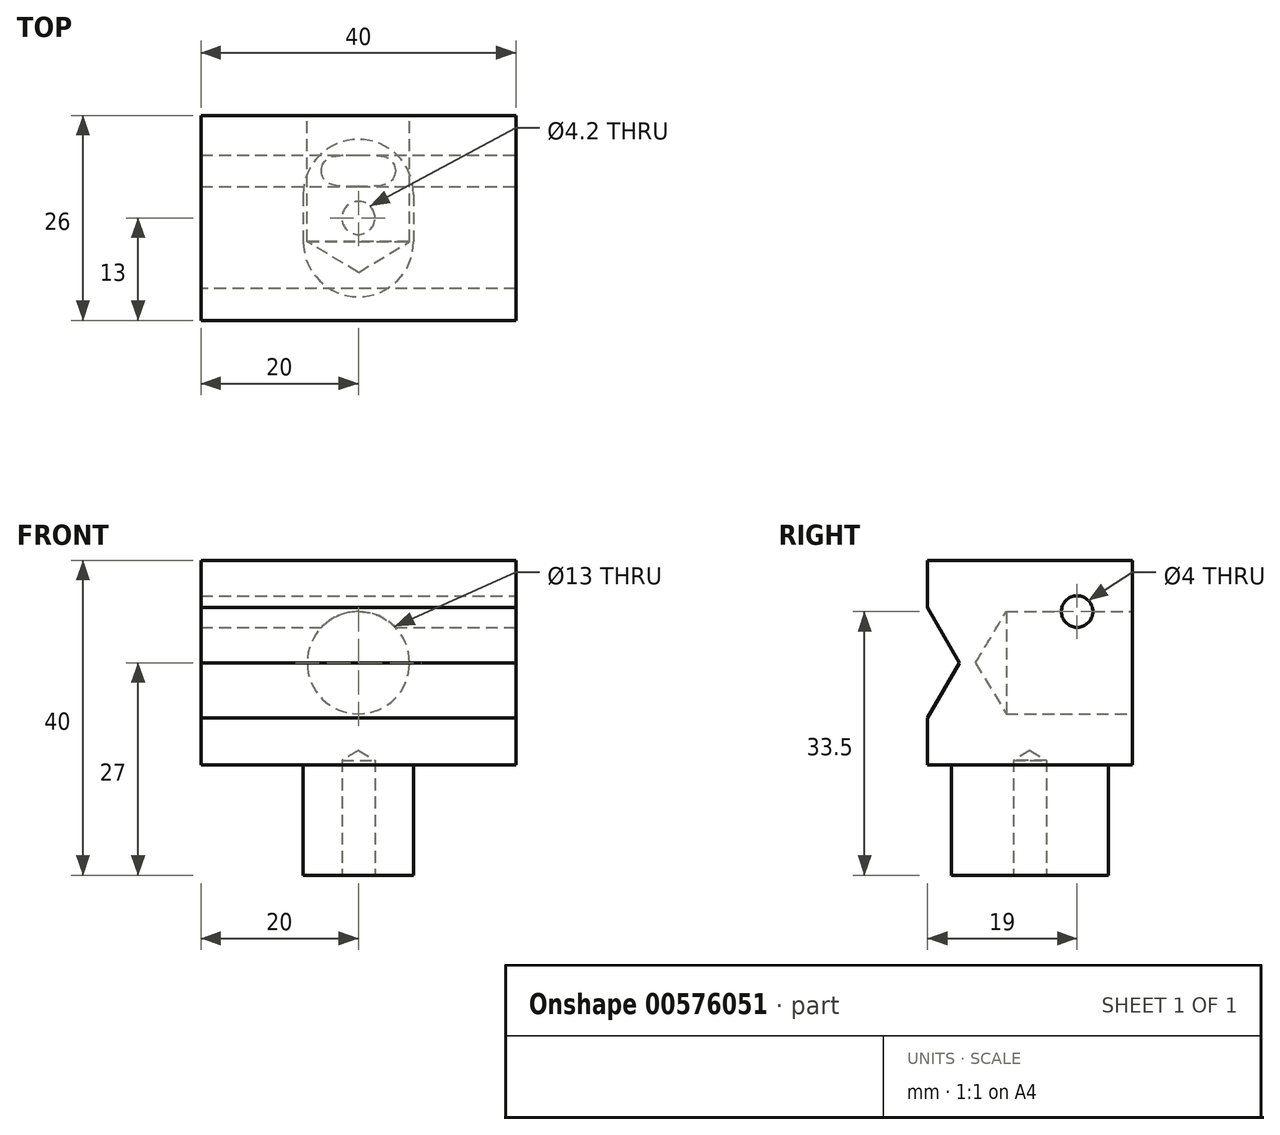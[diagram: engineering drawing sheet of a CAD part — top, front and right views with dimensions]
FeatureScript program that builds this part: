
annotation { "Feature Type Name" : "Feature", "Feature Type Description" : "" }
export const myFeature = defineFeature(function(context is Context, id is Id, definition is map)
    precondition{}
    {
        {
            var Q0;
            Q0=qCreatedBy(makeId("Right.planeOp"),FACE);
            var sketch = newSketch(context, id + "F0", { "sketchPlane" : qUnion([Q0])});
            skLineSegment(sketch, "E0.bottom", {"start": v(13, -13) * mm, "end": v(-13, -13) * mm});
            skLineSegment(sketch, "E0.top", {"start": v(13, 13) * mm, "end": v(-13, 13) * mm});
            skLineSegment(sketch, "E0.left", {"start": v(13, -13) * mm, "end": v(13, 13) * mm});
            skLineSegment(sketch, "E0.right", {"start": v(-13, -13) * mm, "end": v(-13, 13) * mm});
            skPoint(sketch, "E0.middle", {"position": v(0, 0) * mm});
            skLineSegment(sketch, "E1", {"start": v(13, 0) * mm, "end": v(-13, 0) * mm, "construction": true});
            skLineSegment(sketch, "E2", {"start": v(-13, 7) * mm, "end": v(-8.96, 0) * mm});
            skLineSegment(sketch, "E3", {"start": v(-8.96, 0) * mm, "end": v(-13, -7) * mm});
            skSolve(sketch);
        }
        {
            var Q0;
            {var subQ1=sQuery(id+"F0.wireOp",EDGE,"E0.bottom");Q0=makeQuery(id+"F0.imprint","IMPRINT",FACE,{"disambiguationData":[TD([[makeQuery(id+"F0.imprint","IMPRINT",EDGE,{"derivedFrom":subQ1}),-1.0]])]});}
            extrude(context, id + "F1", {"entities" : qUnion([Q0]), "endBound" : BoundingType.SYMMETRIC, "depth" : 40 * mm, "offsetDistance" : 25 * mm});
        }
        {
            var Q0;
            Q0=makeQuery(id+"F1.opExtrude","SWEPT_FACE",FACE,{"disambiguationData":[OSD([sQuery(id+"F0.wireOp",EDGE,"E0.bottom")])]});
            var sketch = newSketch(context, id + "F2", { "sketchPlane" : qUnion([Q0])});
            skLineSegment(sketch, "E4.bottom", {"start": v(7, -10) * mm, "end": v(-7, -10) * mm});
            skLineSegment(sketch, "E4.top", {"start": v(7, 10) * mm, "end": v(-7, 10) * mm});
            skLineSegment(sketch, "E4.left", {"start": v(7, -10) * mm, "end": v(7, 10) * mm});
            skLineSegment(sketch, "E4.right", {"start": v(-7, -10) * mm, "end": v(-7, 10) * mm});
            skPoint(sketch, "E4.middle", {"position": v(0, 0) * mm});
            skSolve(sketch);
        }
        {
            var Q0;
            Q0=makeQuery(id+"F2.imprint","IMPRINT",FACE,{"disambiguationData":[TD([[makeQuery(id+"F2.imprint","IMPRINT",EDGE,{"derivedFrom":sQuery(id+"F2.wireOp",EDGE,"E4.bottom")}),-1.0]])]});
            extrude(context, id + "F3", {"entities" : qUnion([Q0]), "operationType" : NewBodyOperationType.ADD, "depth" : 14 * mm, "offsetDistance" : 25 * mm});
        }
        {
            var Q0;
            Q0=makeQuery(id+"F3.opExtrude","SWEPT_EDGE",EDGE,{"disambiguationData":[OSD([sQuery(id+"F2.wireOp",EDGE,"E4.top"),sQuery(id+"F2.wireOp",EDGE,"E4.left")])]});
            var Q1;
            Q1=makeQuery(id+"F3.opExtrude","SWEPT_EDGE",EDGE,{"disambiguationData":[OSD([sQuery(id+"F2.wireOp",EDGE,"E4.top"),sQuery(id+"F2.wireOp",EDGE,"E4.right")])]});
            var Q2;
            Q2=makeQuery(id+"F3.opExtrude","SWEPT_EDGE",EDGE,{"disambiguationData":[OSD([sQuery(id+"F2.wireOp",EDGE,"E4.bottom"),sQuery(id+"F2.wireOp",EDGE,"E4.left")])]});
            var Q3;
            Q3=makeQuery(id+"F3.opExtrude","SWEPT_EDGE",EDGE,{"disambiguationData":[OSD([sQuery(id+"F2.wireOp",EDGE,"E4.bottom"),sQuery(id+"F2.wireOp",EDGE,"E4.right")])]});
            fillet(context, id + "F4", {"entities" : qUnion([Q0, Q1, Q2, Q3]), "radius" : 7 * mm, "tangentPropagation" : true, "allowEdgeOverflow" : false});
        }
        {
            var Q0;
            Q0=makeQuery(id+"F1.opExtrude","SWEPT_FACE",FACE,{"disambiguationData":[OSD([sQuery(id+"F0.wireOp",EDGE,"E0.left")])]});
            var sketch = newSketch(context, id + "F5", { "sketchPlane" : qUnion([Q0])});
            skPoint(sketch, "E5.0", {"position": v(0, 0) * mm});
            skSolve(sketch);
        }
        {
            var Q0;
            Q0=sQuery(id+"F5.wireOp",VERTEX,"E5.0");
            var Q1;
            Q1=makeQuery(id+"F1.opExtrude","SWEPT_BODY",BODY,{"disambiguationData":[OSD([sQuery(id+"F0.wireOp",EDGE,"E0.bottom"),sQuery(id+"F0.wireOp",EDGE,"E0.top"),sQuery(id+"F0.wireOp",EDGE,"E0.left"),sQuery(id+"F0.wireOp",EDGE,"E0.right"),sQuery(id+"F0.wireOp",EDGE,"E2"),sQuery(id+"F0.wireOp",EDGE,"E3")])]});
            hole(context, id + "F6", {"style" : HoleStyle.SIMPLE, "endStyle" : HoleEndStyle.BLIND, "holeDiameter" : 13 * mm, "holeDepth" : 16 * mm, "isTappedThrough" : true, "tappedDepth" : 12 * mm, "tapClearance" : 3, "locations" : qUnion([Q0]), "scope" : qUnion([Q1])});
        }
        {
            var Q0;
            Q0=qCreatedBy(makeId("Right.planeOp"),FACE);
            var sketch = newSketch(context, id + "F7", { "sketchPlane" : qUnion([Q0])});
            skCircle(sketch, "E6", {"center": v(6, 6.5) * mm, "radius": 2 * mm});
            skSolve(sketch);
        }
        {
            var Q0;
            Q0=makeQuery(id+"F7.imprint","IMPRINT",FACE,{"disambiguationData":[TD([[makeQuery(id+"F7.imprint","IMPRINT",EDGE,{"derivedFrom":sQuery(id+"F7.wireOp",EDGE,"E6")}),1.0]])]});
            extrude(context, id + "F8", {"entities" : qUnion([Q0]), "operationType" : NewBodyOperationType.REMOVE, "endBound" : BoundingType.SYMMETRIC, "oppositeDirection" : true, "depth" : 40 * mm, "offsetDistance" : 25 * mm});
        }
        {
            var Q0;
            Q0=makeQuery(id+"F3.opExtrude","CAP_FACE",FACE,{"disambiguationData":[OSD([sQuery(id+"F2.wireOp",EDGE,"E4.bottom"),sQuery(id+"F2.wireOp",EDGE,"E4.top"),sQuery(id+"F2.wireOp",EDGE,"E4.left"),sQuery(id+"F2.wireOp",EDGE,"E4.right")])],"isStart":false});
            var sketch = newSketch(context, id + "F9", { "sketchPlane" : qUnion([Q0])});
            skPoint(sketch, "E7.0", {"position": v(0, 0) * mm});
            skSolve(sketch);
        }
        {
            var Q0;
            Q0=sQuery(id+"F9.wireOp",VERTEX,"E7.0");
            var Q1;
            Q1=makeQuery(id+"F1.opExtrude","SWEPT_BODY",BODY,{"disambiguationData":[OSD([sQuery(id+"F0.wireOp",EDGE,"E0.bottom"),sQuery(id+"F0.wireOp",EDGE,"E0.top"),sQuery(id+"F0.wireOp",EDGE,"E0.left"),sQuery(id+"F0.wireOp",EDGE,"E0.right"),sQuery(id+"F0.wireOp",EDGE,"E2"),sQuery(id+"F0.wireOp",EDGE,"E3")])]});
            hole(context, id + "F10", {"style" : HoleStyle.SIMPLE, "endStyle" : HoleEndStyle.BLIND, "standardTappedOrClearance" : lookupTablePath({ "standard" : "ISO", "engagement" : "75%", "pitch" : "0.8 mm", "size" : "M5", "type" : "Tapped" }), "standardBlindInLast" : lookupTablePath({ "standard" : "ISO", "engagement" : "75%", "pitch" : "0.8 mm", "size" : "M5", "type" : "Tapped" }), "holeDiameter" : 4.2 * mm, "showTappedDepth" : true, "holeDepth" : 14.6 * mm, "isTappedThrough" : true, "tappedDepth" : 13 * mm, "tapClearance" : 2, "locations" : qUnion([Q0]), "scope" : qUnion([Q1]), "majorDiameter" : 5 * mm});
        }
    });
